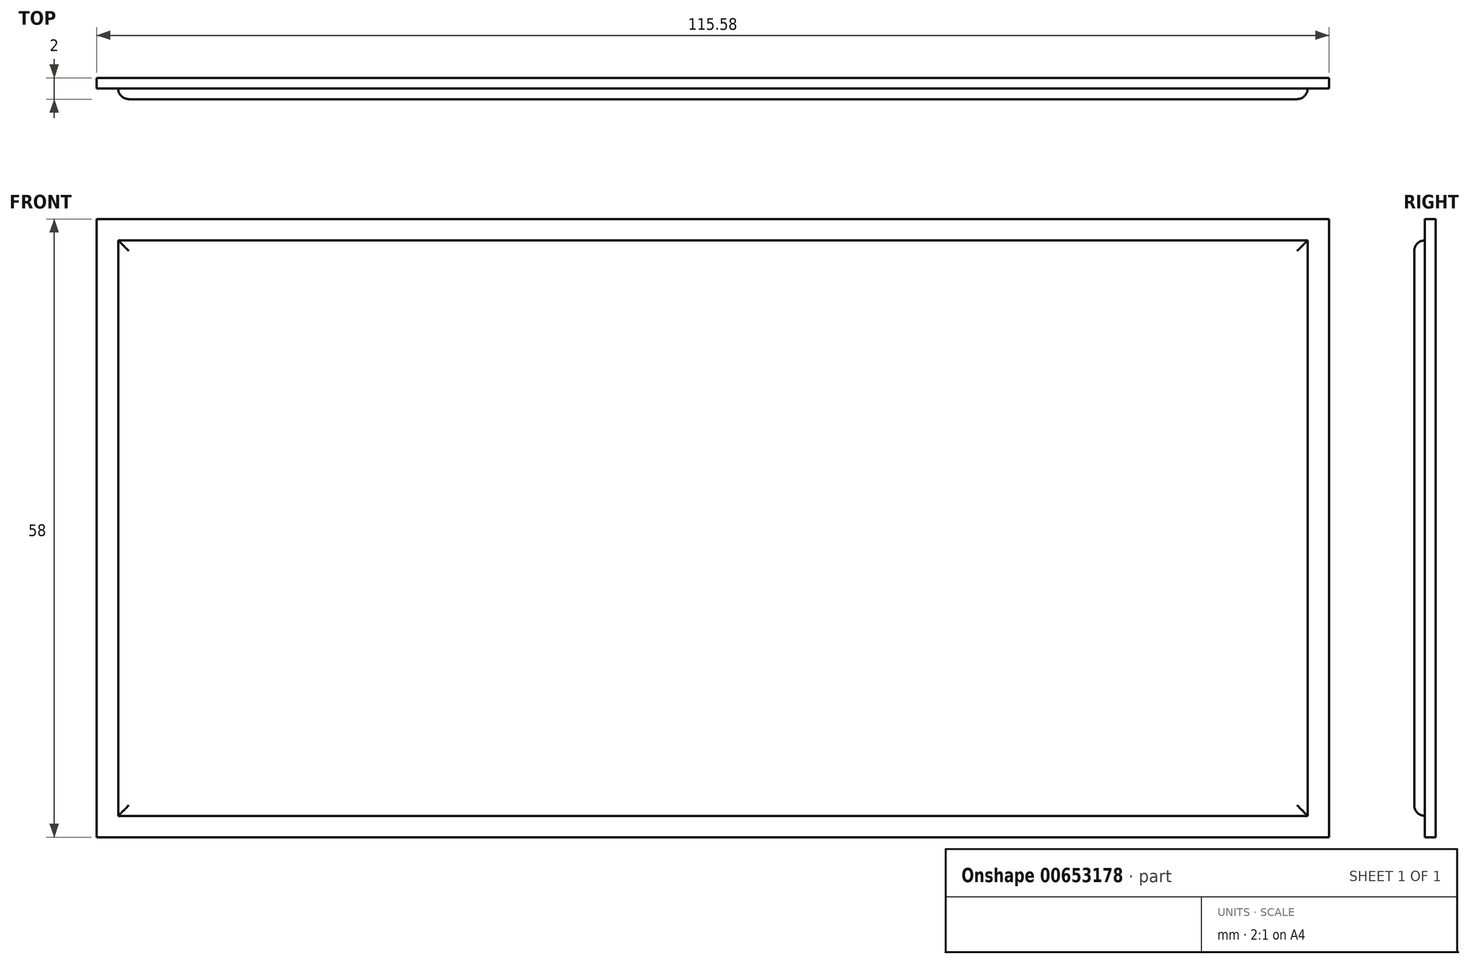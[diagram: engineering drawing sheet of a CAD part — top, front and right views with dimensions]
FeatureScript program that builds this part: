
annotation { "Feature Type Name" : "Feature", "Feature Type Description" : "" }
export const myFeature = defineFeature(function(context is Context, id is Id, definition is map)
    precondition{}
    {
        {
            var Q0;
            Q0=qCreatedBy(makeId("Front.planeOp"),FACE);
            var sketch = newSketch(context, id + "F0", { "sketchPlane" : qUnion([Q0])});
            skLineSegment(sketch, "E0.bottom", {"start": v(0, 0) * mm, "end": v(115.58, 0) * mm});
            skLineSegment(sketch, "E0.top", {"start": v(0, 58) * mm, "end": v(115.58, 58) * mm});
            skLineSegment(sketch, "E0.left", {"start": v(0, 0) * mm, "end": v(0, 58) * mm});
            skLineSegment(sketch, "E0.right", {"start": v(115.58, 0) * mm, "end": v(115.58, 58) * mm});
            skSolve(sketch);
        }
        {
            var Q0;
            Q0=makeQuery(id+"F0.imprint","IMPRINT",FACE,{"disambiguationData":[TD([[makeQuery(id+"F0.imprint","IMPRINT",EDGE,{"derivedFrom":sQuery(id+"F0.wireOp",EDGE,"E0.bottom")}),1.0]])]});
            var Q1;
            Q1=makeQuery(id+"F0.imprint","IMPRINT",FACE,{"disambiguationData":[TD([[makeQuery(id+"F0.imprint","IMPRINT",EDGE,{"derivedFrom":sQuery(id+"F0.wireOp",EDGE,"hJACW9QR-VTGb-IF7w-Slkk-mPvcegFV5SWE.bottom")}),1.0]])]});
            extrude(context, id + "F1", {"entities" : qUnion([Q0, Q1]), "depth" : 1 * mm, "offsetDistance" : 25.4 * mm});
        }
        {
            var Q0;
            Q0=makeQuery(id+"F1.opExtrude","CAP_FACE",FACE,{"disambiguationData":[OSD([sQuery(id+"F0.wireOp",EDGE,"E0.bottom"),sQuery(id+"F0.wireOp",EDGE,"E0.top"),sQuery(id+"F0.wireOp",EDGE,"E0.left"),sQuery(id+"F0.wireOp",EDGE,"E0.right")])],"isStart":false});
            var sketch = newSketch(context, id + "F2", { "sketchPlane" : qUnion([Q0])});
            skLineSegment(sketch, "E1.bottom", {"start": v(2, 2) * mm, "end": v(113.58, 2) * mm});
            skLineSegment(sketch, "E1.top", {"start": v(2, 56) * mm, "end": v(113.58, 56) * mm});
            skLineSegment(sketch, "E1.left", {"start": v(2, 2) * mm, "end": v(2, 56) * mm});
            skLineSegment(sketch, "E1.right", {"start": v(113.58, 2) * mm, "end": v(113.58, 56) * mm});
            skSolve(sketch);
        }
        {
            var Q0;
            Q0=makeQuery(id+"F2.imprint","IMPRINT",FACE,{"disambiguationData":[TD([[makeQuery(id+"F2.imprint","IMPRINT",EDGE,{"derivedFrom":sQuery(id+"F2.wireOp",EDGE,"E1.bottom")}),1.0]])]});
            extrude(context, id + "F3", {"entities" : qUnion([Q0]), "operationType" : NewBodyOperationType.ADD, "depth" : 1 * mm, "offsetDistance" : 25.4 * mm});
        }
        {
            var Q0;
            Q0=makeQuery(id+"F3.opExtrude","CAP_EDGE",EDGE,{"disambiguationData":[OSD([sQuery(id+"F2.wireOp",EDGE,"E1.top")])],"isStart":false});
            var Q1;
            Q1=makeQuery(id+"F3.opExtrude","CAP_EDGE",EDGE,{"disambiguationData":[OSD([sQuery(id+"F2.wireOp",EDGE,"E1.left")])],"isStart":false});
            var Q2;
            Q2=makeQuery(id+"F3.opExtrude","CAP_EDGE",EDGE,{"disambiguationData":[OSD([sQuery(id+"F2.wireOp",EDGE,"E1.bottom")])],"isStart":false});
            var Q3;
            Q3=makeQuery(id+"F3.opExtrude","CAP_EDGE",EDGE,{"disambiguationData":[OSD([sQuery(id+"F2.wireOp",EDGE,"E1.right")])],"isStart":false});
            fillet(context, id + "F4", {"entities" : qUnion([Q0, Q1, Q2, Q3]), "radius" : 1 * mm, "tangentPropagation" : true, "allowEdgeOverflow" : false});
        }
    });
